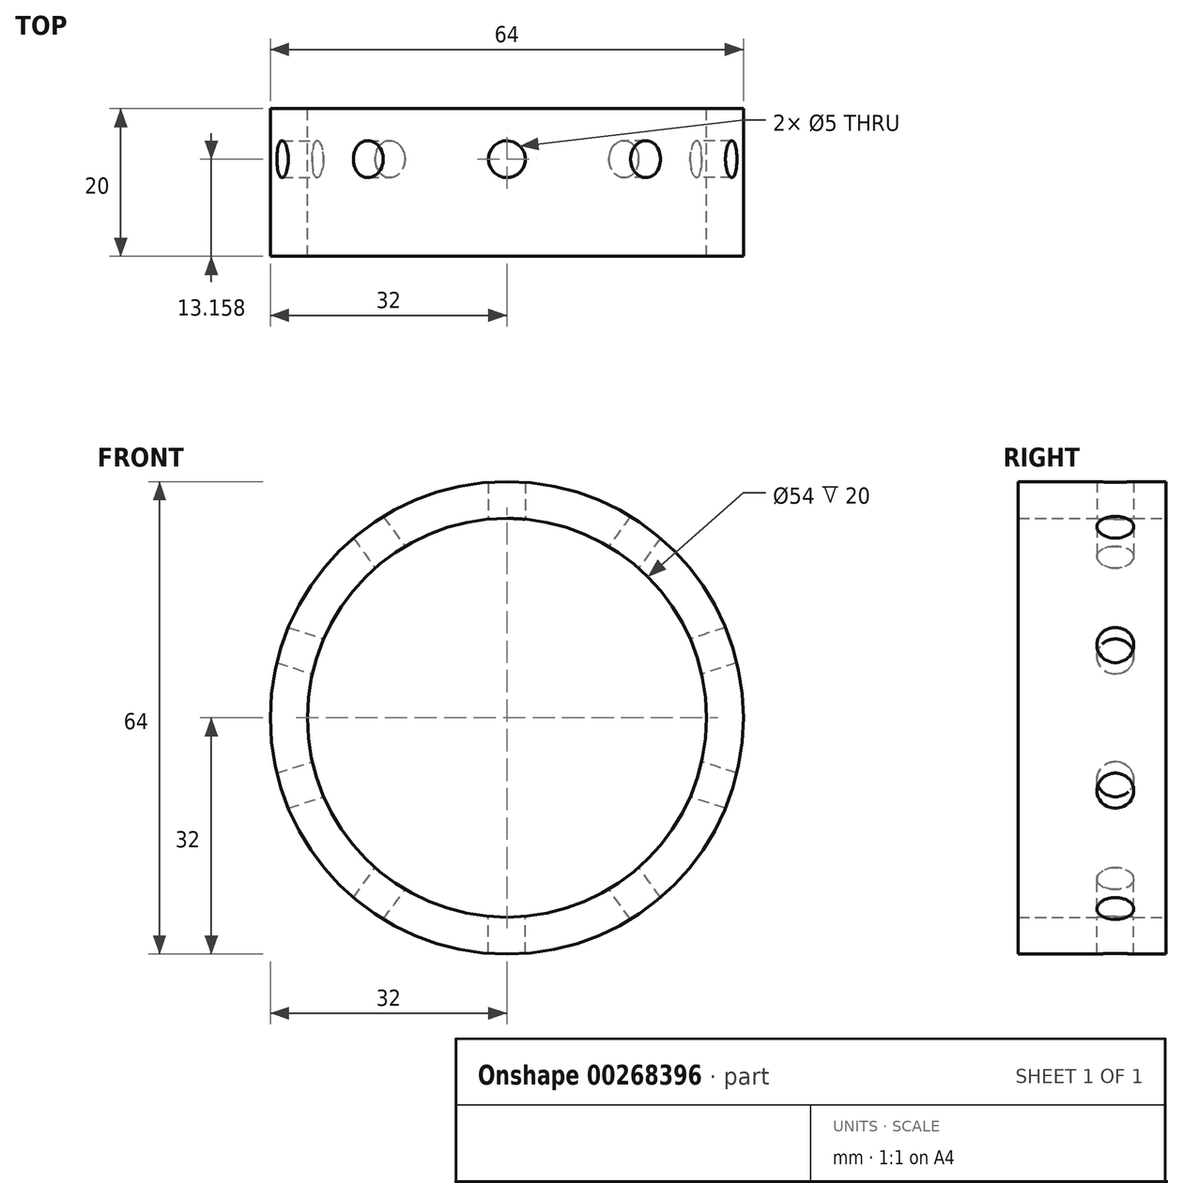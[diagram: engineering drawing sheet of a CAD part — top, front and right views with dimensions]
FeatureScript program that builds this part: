
annotation { "Feature Type Name" : "Feature", "Feature Type Description" : "" }
export const myFeature = defineFeature(function(context is Context, id is Id, definition is map)
    precondition{}
    {
        {
            var Q0;
            Q0=qCreatedBy(makeId("Front.planeOp"),FACE);
            var sketch = newSketch(context, id + "F0", { "sketchPlane" : qUnion([Q0])});
            skCircle(sketch, "E0", {"center": v(0, 0) * mm, "radius": 32 * mm});
            skLineSegment(sketch, "E1", {"start": v(0, 32) * mm, "end": v(0, -32) * mm});
            skSolve(sketch);
        }
        {
            var Q0;
            Q0=makeQuery(id+"F0.imprint","IMPRINT",FACE,{"disambiguationData":[TD([[makeQuery(id+"F0.imprint","IMPRINT",EDGE,{"derivedFrom":sQuery(id+"F0.wireOp",EDGE,"E0")}),1.0]])]});
            extrude(context, id + "F1", {"entities" : qUnion([Q0]), "depth" : 20 * mm, "offsetDistance" : 25 * mm});
        }
        {
            var Q0;
            Q0=qCreatedBy(makeId("Top.planeOp"),FACE);
            var sketch = newSketch(context, id + "F2", { "sketchPlane" : qUnion([Q0])});
            skCircle(sketch, "E2", {"center": v(0, -6.84) * mm, "radius": 2.5 * mm});
            skSolve(sketch);
        }
        {
            var Q0;
            Q0 = qSketchRegion(id + "F2", true);
            extrude(context, id + "F3", {"entities" : qUnion([Q0]), "depth" : 50 * mm, "offsetDistance" : 25 * mm});
        }
        {
            var Q0;
            Q0=makeQuery(id+"F1.opExtrude","CAP_FACE",FACE,{"disambiguationData":[OSD([sQuery(id+"F0.wireOp",EDGE,"E0")])],"isStart":true});
            var sketch = newSketch(context, id + "F4", { "sketchPlane" : qUnion([Q0])});
            skCircle(sketch, "E3", {"center": v(0, 0) * mm, "radius": 32 * mm});
            skCircle(sketch, "E4", {"center": v(0, 0) * mm, "radius": 27 * mm});
            skSolve(sketch);
        }
        {
            var Q0;
            Q0=makeQuery(id+"F4.imprint","IMPRINT",FACE,{"disambiguationData":[TD([[makeQuery(id+"F4.imprint","IMPRINT",EDGE,{"derivedFrom":sQuery(id+"F4.wireOp",EDGE,"E3")}),-1.0]])]});
            extrude(context, id + "F5", {"entities" : qUnion([Q0]), "operationType" : NewBodyOperationType.INTERSECT, "oppositeDirection" : true, "depth" : 25 * mm, "offsetDistance" : 25 * mm});
        }
        {
            var Q0;
            Q0=makeQuery(id+"F3.opExtrude","SWEPT_BODY",BODY,{"disambiguationData":[OSD([sQuery(id+"F2.wireOp",EDGE,"E2")])]});
            var Q1;
            Q1=makeQuery(id+"F1.opExtrude","SWEPT_BODY",BODY,{"disambiguationData":[OSD([sQuery(id+"F0.wireOp",EDGE,"E0")])]});
            booleanBodies(context, id + "F6", {"operationType" : BooleanOperationType.SUBTRACTION, "tools" : qUnion([Q0]), "targets" : qUnion([Q1])});
        }
        {
            var Q0;
            Q0=makeQuery(id+"F6.opBoolean","COPY",FACE,{"derivedFrom":makeQuery(id+"F3.opExtrude","SWEPT_FACE",FACE,{"disambiguationData":[OSD([sQuery(id+"F2.wireOp",EDGE,"E2")])]})});
            var Q1;
            Q1=makeQuery(id+"F6.opBoolean","COPY",FACE,{"derivedFrom":makeQuery(id+"F5.boolean.opBoolean","COPY",FACE,{"derivedFrom":makeQuery(id+"F5.boolean.toolComplement.opBoolean","COPY",FACE,{"derivedFrom":makeQuery(id+"F5.opExtrude","SWEPT_FACE",FACE,{"disambiguationData":[OSD([sQuery(id+"F4.wireOp",EDGE,"E4")])]})})})});
            var Q2;
            Q2=makeQuery(id+"F1.opExtrude","SWEPT_FACE",FACE,{"disambiguationData":[OSD([sQuery(id+"F0.wireOp",EDGE,"E0")])]});
            circularPattern(context, id + "F7", {"patternType" : PatternType.FACE, "faces" : qUnion([Q0, Q1]), "axis" : qUnion([Q2]), "angle" : 360 * degree, "instanceCount" : 10, "equalSpace" : true});
        }
    });
